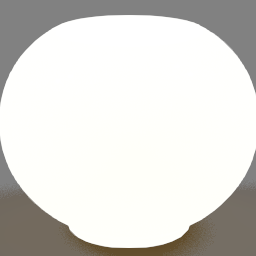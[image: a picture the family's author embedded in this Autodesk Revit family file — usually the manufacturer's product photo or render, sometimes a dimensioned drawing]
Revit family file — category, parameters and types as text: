
# Revit family: 3-100X-xx Deca Mirror
name_source: partatom
category: Luminarias
units: mm (PartAtom-declared; Revit-internal decimal feet)

## family parameters
Anfitrión = Muro
Compartido = No
Corte con vacíos al cargar = No
Cota de conector redondo = Diámetro de uso
Número OmniClass = 23.80.70.00
Origen de luz = No
Punto de cálculo de habitación = No
Siempre vertical = Sí
Tipo de pieza = Normal
Título OmniClass = Lighting

## types (4) — shared parameters
Fabricante = Vanita by Oxygen
Lámpara = LED Array
Metal Finish 1 = 15 - Black
Modelo = 3-100X-xx / Deca
References = Ref. 3 = 120 V / Ref. 37 = 277 V
URL = www.oxygenlighting.com
Voltage = 120 V
Voltage Input = 120 V or 277 V - 50/60 Hz
zero-valued in all types: Elevación por defecto

## per-type parameters (varying)
| type | Comentarios de vataje | Height | Switch | Width |
| 3-1001-15 / Black | 1 x 39.4 W at 120 V | 580 mm  [stored 1.90289 ft] | 576 mm | 610 mm |
| 3-1002-15 / Black | 1 x 57.7 W at 120 V | 726 mm  [stored 2.38189 ft] | 722 mm | 763 mm |
| 3-1003-15 / Black | 1 x 75.7 W at 120 V | 869 mm | 865 mm | 914 mm |
| 3-1004-15 / Black | 1 x 99.6 W at 120 V | 1161 mm  [stored 3.80906 ft] | 1157 mm | 1221 mm |

note: [stored X ft] marks values corroborated as IEEE doubles in the binary element streams (Revit-internal decimal feet)

## geometry (parser evidence)
native form markers: Sweep x6
no freeform markers — native parametric forms only
